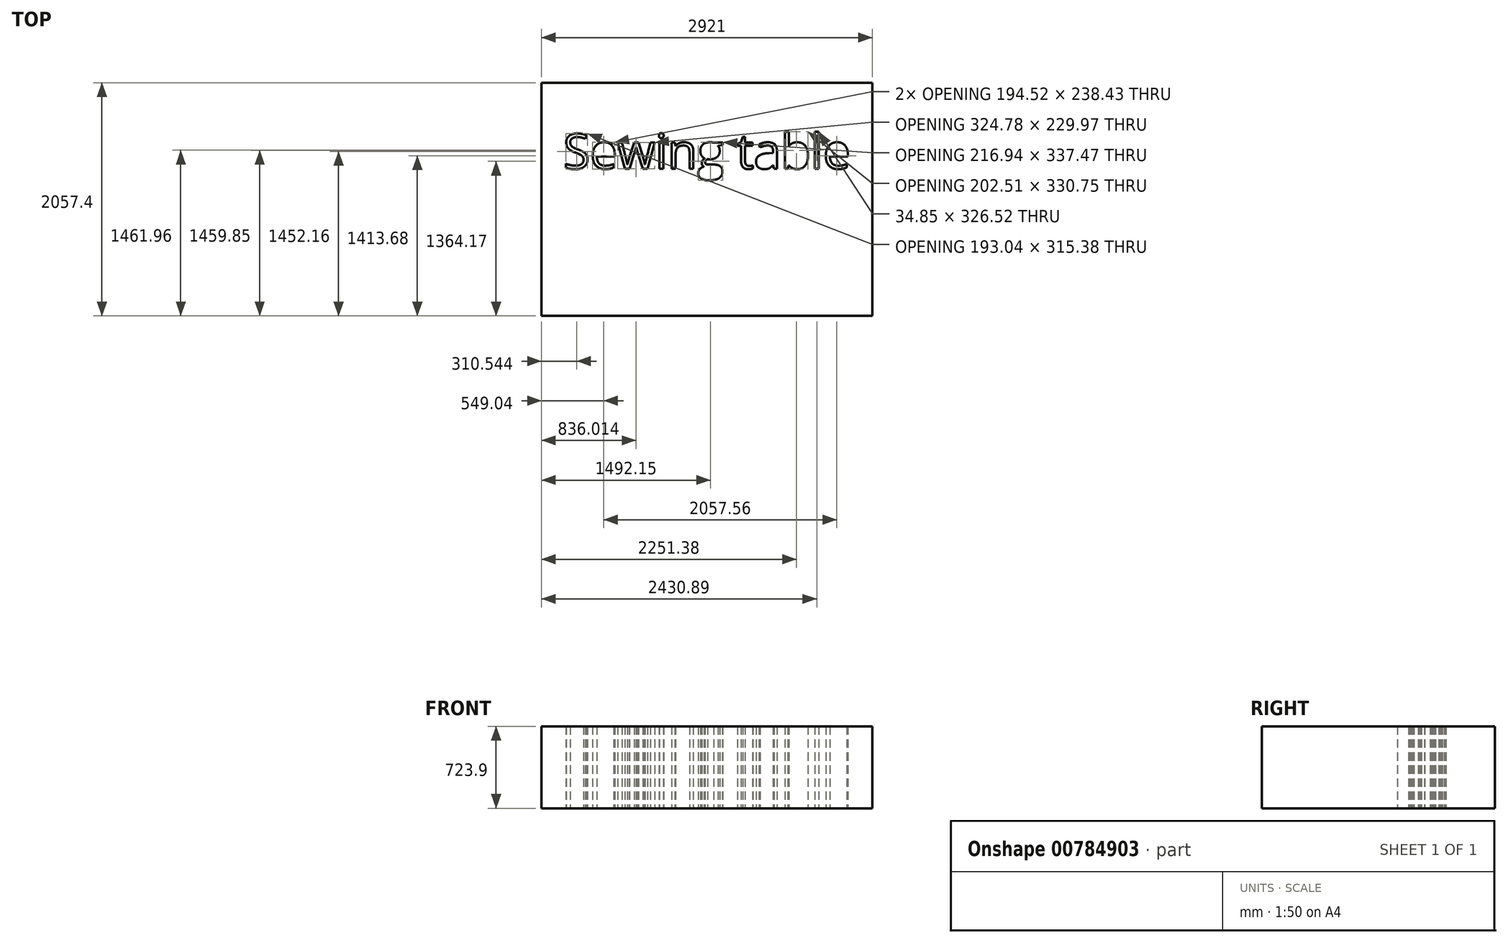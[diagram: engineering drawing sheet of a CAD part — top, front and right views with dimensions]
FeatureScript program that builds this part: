
annotation { "Feature Type Name" : "Feature", "Feature Type Description" : "" }
export const myFeature = defineFeature(function(context is Context, id is Id, definition is map)
    precondition{}
    {
        {
            var Q0;
            Q0=qCreatedBy(makeId("Top.planeOp"),FACE);
            var sketch = newSketch(context, id + "F0", { "sketchPlane" : qUnion([Q0])});
            skLineSegment(sketch, "E0.bottom", {"start": v(1460.5, 1028.7) * mm, "end": v(-1460.5, 1028.7) * mm});
            skLineSegment(sketch, "E0.top", {"start": v(1460.5, -1028.7) * mm, "end": v(-1460.5, -1028.7) * mm});
            skLineSegment(sketch, "E0.left", {"start": v(1460.5, 1028.7) * mm, "end": v(1460.5, -1028.7) * mm});
            skLineSegment(sketch, "E0.right", {"start": v(-1460.5, 1028.7) * mm, "end": v(-1460.5, -1028.7) * mm});
            skPoint(sketch, "E0.middle", {"position": v(0, 0) * mm});
            skText(sketch, "E1", { "text": "Sewing table", "fontName": "OpenSans-Regular.ttf"});
            const initialGuessF0  = {"E1": [-1.2687, 0.27, 1, 0, 0.3094]};
            skSetInitialGuess(sketch, initialGuessF0);
            skSolve(sketch);
        }
        {
            var Q0;
            Q0=makeQuery(id+"F0.imprint","IMPRINT",FACE,{"disambiguationData":[TD([[makeQuery(id+"F0.imprint","IMPRINT",EDGE,{"derivedFrom":sQuery(id+"F0.wireOp",EDGE,"E0.bottom")}),1.0]])]});
            extrude(context, id + "F1", {"entities" : qUnion([Q0]), "depth" : 723.9 * mm, "offsetDistance" : 25.4 * mm});
        }
    });
